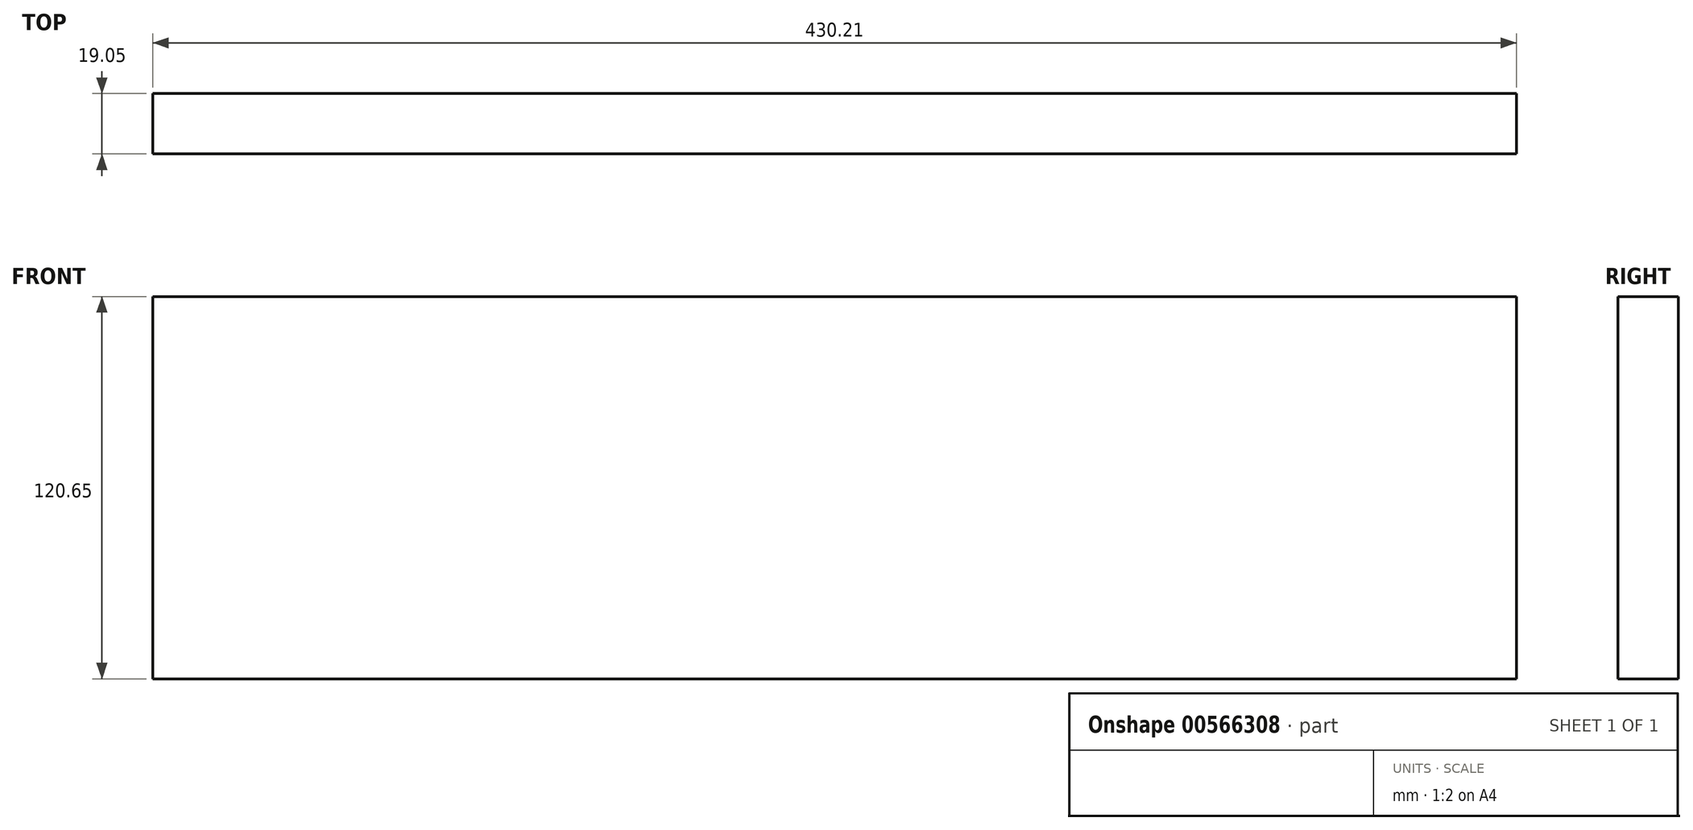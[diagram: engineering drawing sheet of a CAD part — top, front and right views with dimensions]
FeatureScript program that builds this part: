
annotation { "Feature Type Name" : "Feature", "Feature Type Description" : "" }
export const myFeature = defineFeature(function(context is Context, id is Id, definition is map)
    precondition{}
    {
        {
            var Q0;
            Q0=qCreatedBy(makeId("Front.planeOp"),FACE);
            var sketch = newSketch(context, id + "F0", { "sketchPlane" : qUnion([Q0])});
            skLineSegment(sketch, "E0.bottom", {"start": v(0, 0) * mm, "end": v(430.21, 0) * mm});
            skLineSegment(sketch, "E0.top", {"start": v(0, 120.65) * mm, "end": v(430.21, 120.65) * mm});
            skLineSegment(sketch, "E0.left", {"start": v(0, 0) * mm, "end": v(0, 120.65) * mm});
            skLineSegment(sketch, "E0.right", {"start": v(430.21, 0) * mm, "end": v(430.21, 120.65) * mm});
            skSolve(sketch);
        }
        {
            var Q0;
            Q0=makeQuery(id+"F0.imprint","IMPRINT",FACE,{"disambiguationData":[TD([[makeQuery(id+"F0.imprint","IMPRINT",EDGE,{"derivedFrom":sQuery(id+"F0.wireOp",EDGE,"E0.bottom")}),1.0]])]});
            extrude(context, id + "F1", {"entities" : qUnion([Q0]), "depth" : 19.05 * mm, "offsetDistance" : 25.4 * mm});
        }
    });
